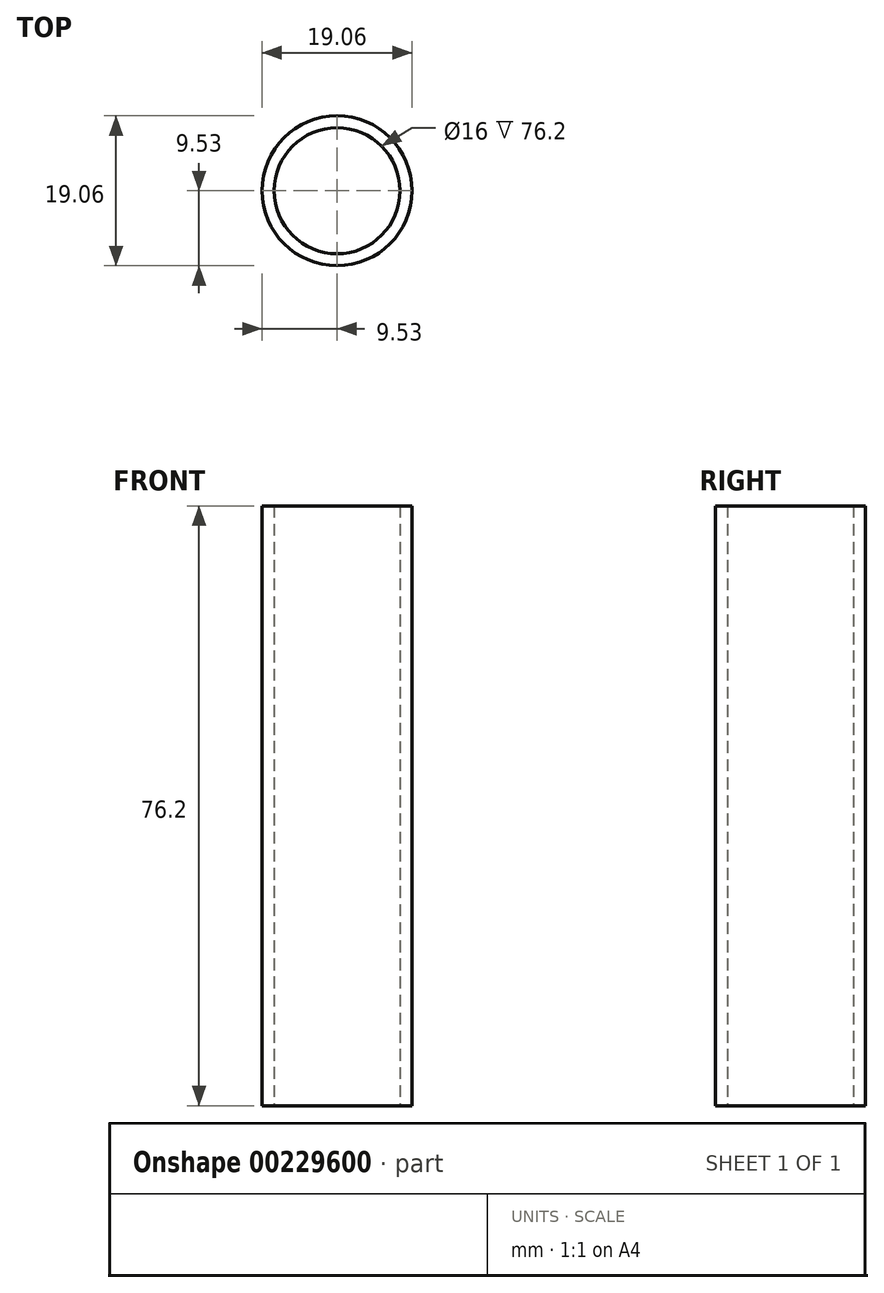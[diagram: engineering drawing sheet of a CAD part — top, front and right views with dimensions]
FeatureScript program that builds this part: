
annotation { "Feature Type Name" : "Feature", "Feature Type Description" : "" }
export const myFeature = defineFeature(function(context is Context, id is Id, definition is map)
    precondition{}
    {
        {
            var Q0;
            Q0=qCreatedBy(makeId("Top.planeOp"),FACE);
            var sketch = newSketch(context, id + "F0", { "sketchPlane" : qUnion([Q0])});
            skCircle(sketch, "E0", {"center": v(0, 0) * mm, "radius": 9.53 * mm});
            skCircle(sketch, "E1", {"center": v(0, 0) * mm, "radius": 8 * mm});
            skSolve(sketch);
        }
        {
            var Q0;
            Q0 = qSketchRegion(id + "F0", true);
            extrude(context, id + "F1", {"entities" : qUnion([Q0]), "depth" : 38.1 * mm, "hasSecondDirection" : true, "secondDirectionOppositeDirection" : true, "secondDirectionDepth" : 38.1 * mm});
        }
    });
